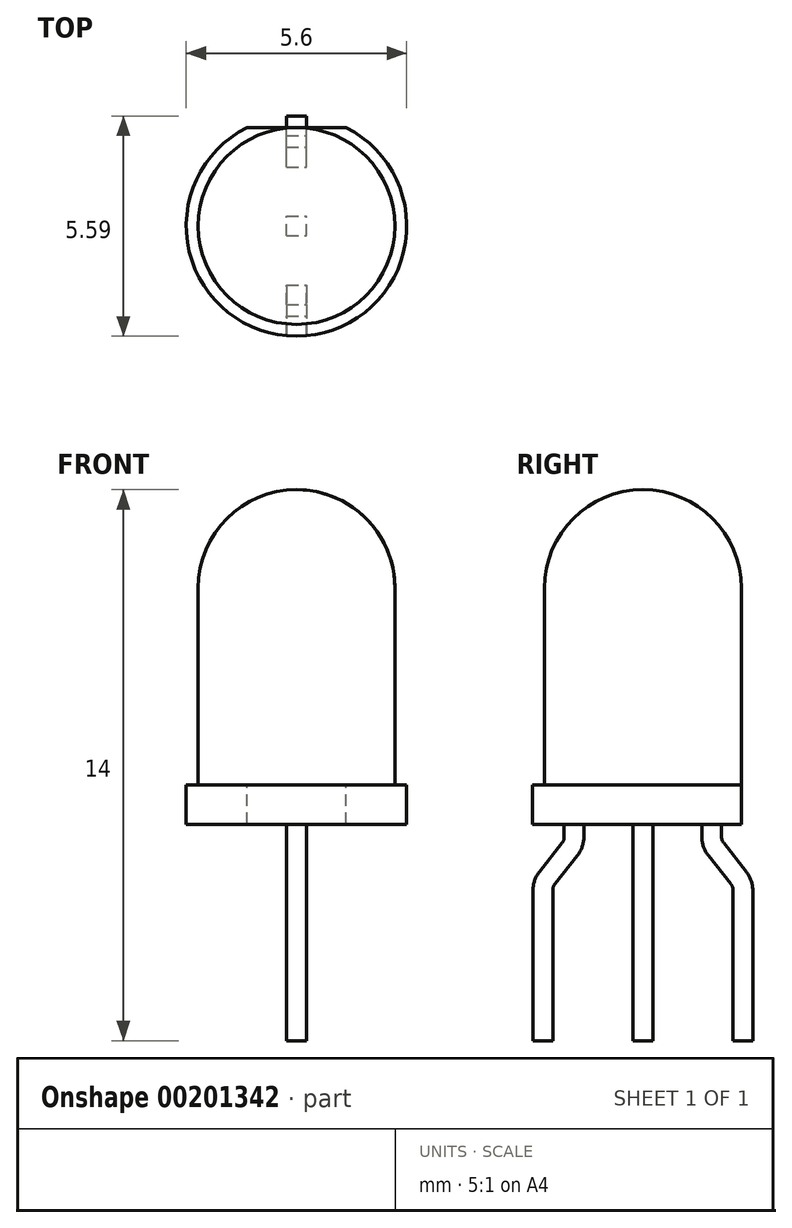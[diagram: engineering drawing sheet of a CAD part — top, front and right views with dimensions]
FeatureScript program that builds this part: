
annotation { "Feature Type Name" : "Feature", "Feature Type Description" : "" }
export const myFeature = defineFeature(function(context is Context, id is Id, definition is map)
    precondition{}
    {
        {
            var Q0;
            Q0=qCreatedBy(makeId("Top.planeOp"),FACE);
            var sketch = newSketch(context, id + "F0", { "sketchPlane" : qUnion([Q0])});
            skCircle(sketch, "E0", {"center": v(0, 0) * mm, "radius": 2.5 * mm});
            skSolve(sketch);
        }
        {
            var Q0;
            Q0=makeQuery(id+"F0.imprint","IMPRINT",FACE,{"disambiguationData":[TD([[makeQuery(id+"F0.imprint","IMPRINT",EDGE,{"derivedFrom":sQuery(id+"F0.wireOp",EDGE,"E0")}),1.0]])]});
            extrude(context, id + "F1", {"entities" : qUnion([Q0]), "depth" : 7.5 * mm});
        }
        {
            var Q0;
            Q0=makeQuery(id+"F1.opExtrude","CAP_EDGE",EDGE,{"disambiguationData":[OSD([sQuery(id+"F0.wireOp",EDGE,"E0")])],"isStart":false});
            fillet(context, id + "F2", {"entities" : qUnion([Q0]), "radius" : 2.5 * mm, "tangentPropagation" : true, "allowEdgeOverflow" : false});
        }
        {
            var Q0;
            Q0=makeQuery(id+"F1.opExtrude","CAP_FACE",FACE,{"disambiguationData":[OSD([sQuery(id+"F0.wireOp",EDGE,"E0")])],"isStart":true});
            var sketch = newSketch(context, id + "F3", { "sketchPlane" : qUnion([Q0])});
            skArc(sketch, "E1", {"start": v(1.26, -2.5) * mm, "mid": v(0, 2.8) * mm, "end": v(-1.26, -2.5) * mm});
            skLineSegment(sketch, "E2", {"start": v(-1.26, -2.5) * mm, "end": v(1.26, -2.5) * mm});
            skSolve(sketch);
        }
        {
            var Q0;
            Q0 = qSketchRegion(id + "F3", true);
            extrude(context, id + "F4", {"entities" : qUnion([Q0]), "operationType" : NewBodyOperationType.ADD, "depth" : 1 * mm});
        }
        {
            var Q0;
            Q0=makeQuery(id+"F4.opExtrude","CAP_FACE",FACE,{"disambiguationData":[OSD([sQuery(id+"F3.wireOp",EDGE,"E1")])],"isStart":false});
            var sketch = newSketch(context, id + "F5", { "sketchPlane" : qUnion([Q0])});
            skLineSegment(sketch, "E3", {"start": v(0, 2.8) * mm, "end": v(0, -2.8) * mm, "construction": true});
            skLineSegment(sketch, "E4", {"start": v(2.8, 0) * mm, "end": v(-2.5, 0) * mm, "construction": true});
            skLineSegment(sketch, "E5.bottom", {"start": v(-0.25, 2) * mm, "end": v(0.25, 2) * mm});
            skLineSegment(sketch, "E5.top", {"start": v(-0.25, 1.5) * mm, "end": v(0.25, 1.5) * mm});
            skLineSegment(sketch, "E5.left", {"start": v(-0.25, 2) * mm, "end": v(-0.25, 1.5) * mm});
            skLineSegment(sketch, "E5.right", {"start": v(0.25, 2) * mm, "end": v(0.25, 1.5) * mm});
            skLineSegment(sketch, "E6.bottom", {"start": v(-0.25, -1.5) * mm, "end": v(0.25, -1.5) * mm});
            skLineSegment(sketch, "E6.top", {"start": v(-0.25, -2) * mm, "end": v(0.25, -2) * mm});
            skLineSegment(sketch, "E6.left", {"start": v(-0.25, -1.5) * mm, "end": v(-0.25, -2) * mm});
            skLineSegment(sketch, "E6.right", {"start": v(0.25, -1.5) * mm, "end": v(0.25, -2) * mm});
            skLineSegment(sketch, "E7.bottom", {"start": v(-0.25, 0.25) * mm, "end": v(0.25, 0.25) * mm});
            skLineSegment(sketch, "E7.top", {"start": v(-0.25, -0.25) * mm, "end": v(0.25, -0.25) * mm});
            skLineSegment(sketch, "E7.left", {"start": v(-0.25, 0.25) * mm, "end": v(-0.25, -0.25) * mm});
            skLineSegment(sketch, "E7.right", {"start": v(0.25, 0.25) * mm, "end": v(0.25, -0.25) * mm});
            skSolve(sketch);
        }
        {
            var Q0;
            Q0=makeQuery(id+"F5.imprint","IMPRINT",FACE,{"disambiguationData":[TD([[makeQuery(id+"F5.imprint","IMPRINT",EDGE,{"derivedFrom":sQuery(id+"F5.wireOp",EDGE,"E7.bottom")}),-1.0]])]});
            extrude(context, id + "F6", {"entities" : qUnion([Q0]), "operationType" : NewBodyOperationType.ADD, "depth" : 5.5 * mm});
        }
        {
            var Q0;
            Q0=qCreatedBy(makeId("Right.planeOp"),FACE);
            var sketch = newSketch(context, id + "F7", { "sketchPlane" : qUnion([Q0])});
            skLineSegment(sketch, "E8", {"start": v(0, 0) * mm, "end": v(0, -3.36) * mm, "construction": true});
            skLineSegment(sketch, "E9.0", {"start": v(-1.75, -1) * mm, "end": v(-1.75, -1.33) * mm});
            skLineSegment(sketch, "E10.0", {"start": v(1.75, -1) * mm, "end": v(1.75, -1.33) * mm});
            skLineSegment(sketch, "E11", {"start": v(-2.9, -1) * mm, "end": v(2.9, -1) * mm, "construction": true});
            skLineSegment(sketch, "E12", {"start": v(-2.54, -2.67) * mm, "end": v(-2.54, -6.5) * mm});
            skLineSegment(sketch, "E13", {"start": v(-2.97, -2.5) * mm, "end": v(2.97, -2.5) * mm, "construction": true});
            skLineSegment(sketch, "E14", {"start": v(-3.42, -6.5) * mm, "end": v(3.42, -6.5) * mm, "construction": true});
            skLineSegment(sketch, "E15", {"start": v(-1.86, -1.64) * mm, "end": v(-2.43, -2.36) * mm});
            skPoint(sketch, "E16.visualSharp", {"position": v(-2.54, -2.5) * mm});
            skArc(sketch, "E16.filletArc", {"start": v(-2.43, -2.36) * mm, "mid": v(-2.51, -2.5) * mm, "end": v(-2.54, -2.67) * mm});
            skPoint(sketch, "E17.visualSharp", {"position": v(-1.75, -1.5) * mm});
            skArc(sketch, "E17.filletArc", {"start": v(-1.86, -1.64) * mm, "mid": v(-1.78, -1.5) * mm, "end": v(-1.75, -1.33) * mm});
            skLineSegment(sketch, "E18", {"start": v(2.54, -6.5) * mm, "end": v(2.54, -2.67) * mm});
            skLineSegment(sketch, "E19", {"start": v(1.86, -1.64) * mm, "end": v(2.43, -2.36) * mm});
            skPoint(sketch, "E20.visualSharp", {"position": v(2.54, -2.5) * mm});
            skArc(sketch, "E20.filletArc", {"start": v(2.54, -2.67) * mm, "mid": v(2.51, -2.5) * mm, "end": v(2.43, -2.36) * mm});
            skPoint(sketch, "E21.visualSharp", {"position": v(1.75, -1.5) * mm});
            skArc(sketch, "E21.filletArc", {"start": v(1.75, -1.33) * mm, "mid": v(1.78, -1.5) * mm, "end": v(1.86, -1.64) * mm});
            skSolve(sketch);
        }
        {
            var Q0;
            Q0=makeQuery(id+"F5.imprint","IMPRINT",FACE,{"disambiguationData":[TD([[makeQuery(id+"F5.imprint","IMPRINT",EDGE,{"derivedFrom":sQuery(id+"F5.wireOp",EDGE,"E5.bottom")}),-1.0]])]});
            var Q1;
            Q1=sQuery(id+"F7.wireOp",EDGE,"E9.0");
            var Q2;
            Q2=sQuery(id+"F7.wireOp",EDGE,"E17.filletArc");
            var Q3;
            Q3=sQuery(id+"F7.wireOp",EDGE,"E15");
            var Q4;
            Q4=sQuery(id+"F7.wireOp",EDGE,"E16.filletArc");
            var Q5;
            Q5=sQuery(id+"F7.wireOp",EDGE,"E12");
            sweep(context, id + "F8", {"operationType" : NewBodyOperationType.ADD, "profiles" : qUnion([Q0]), "path" : qUnion([Q1, Q2, Q3, Q4, Q5])});
        }
        {
            var Q0;
            Q0=makeQuery(id+"F5.imprint","IMPRINT",FACE,{"disambiguationData":[TD([[makeQuery(id+"F5.imprint","IMPRINT",EDGE,{"derivedFrom":sQuery(id+"F5.wireOp",EDGE,"E6.bottom")}),-1.0]])]});
            var Q1;
            Q1=sQuery(id+"F7.wireOp",EDGE,"E10.0");
            var Q2;
            Q2=sQuery(id+"F7.wireOp",EDGE,"E21.filletArc");
            var Q3;
            Q3=sQuery(id+"F7.wireOp",EDGE,"E19");
            var Q4;
            Q4=sQuery(id+"F7.wireOp",EDGE,"E20.filletArc");
            var Q5;
            Q5=sQuery(id+"F7.wireOp",EDGE,"E18");
            sweep(context, id + "F9", {"operationType" : NewBodyOperationType.ADD, "profiles" : qUnion([Q0]), "path" : qUnion([Q1, Q2, Q3, Q4, Q5])});
        }
    });
